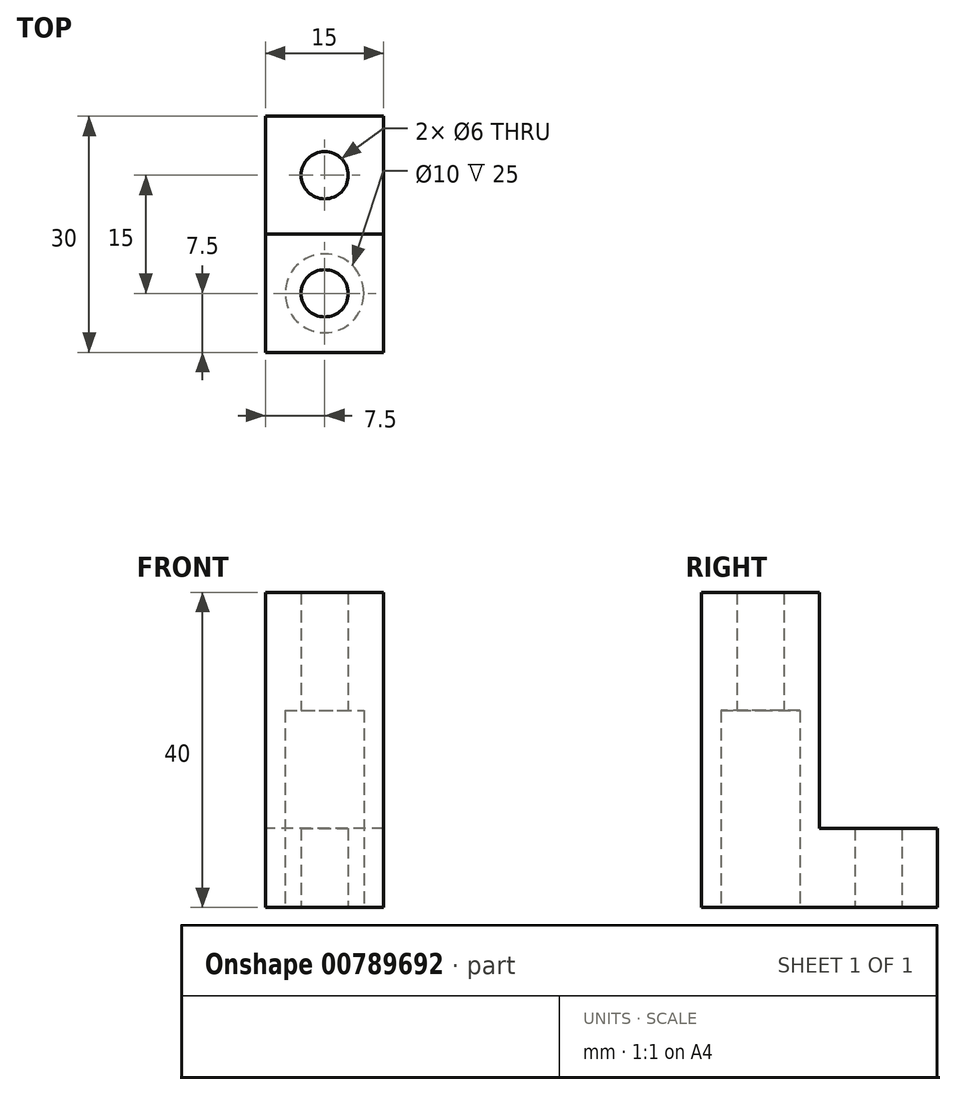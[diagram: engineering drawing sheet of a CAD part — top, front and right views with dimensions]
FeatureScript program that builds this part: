
annotation { "Feature Type Name" : "Feature", "Feature Type Description" : "" }
export const myFeature = defineFeature(function(context is Context, id is Id, definition is map)
    precondition{}
    {
        {
            var Q0;
            Q0=qCreatedBy(makeId("Top.planeOp"),FACE);
            var sketch = newSketch(context, id + "F0", { "sketchPlane" : qUnion([Q0])});
            skLineSegment(sketch, "E0.bottom", {"start": v(7.5, -7.5) * mm, "end": v(-7.5, -7.5) * mm});
            skLineSegment(sketch, "E0.top", {"start": v(7.5, 7.5) * mm, "end": v(-7.5, 7.5) * mm});
            skLineSegment(sketch, "E0.left", {"start": v(7.5, -7.5) * mm, "end": v(7.5, 7.5) * mm});
            skLineSegment(sketch, "E0.right", {"start": v(-7.5, -7.5) * mm, "end": v(-7.5, 7.5) * mm});
            skPoint(sketch, "E0.middle", {"position": v(0, 0) * mm});
            skCircle(sketch, "E1", {"center": v(0, 0) * mm, "radius": 3 * mm});
            skSolve(sketch);
        }
        {
            var Q0;
            Q0 = qSketchRegion(id + "F0", true);
            extrude(context, id + "F1", {"entities" : qUnion([Q0]), "depth" : 40 * mm, "offsetDistance" : 25 * mm});
        }
        {
            var Q0;
            Q0=makeQuery(id+"F1.opExtrude","CAP_FACE",FACE,{"disambiguationData":[OSD([sQuery(id+"F0.wireOp",EDGE,"E0.bottom"),sQuery(id+"F0.wireOp",EDGE,"E0.top"),sQuery(id+"F0.wireOp",EDGE,"E0.left"),sQuery(id+"F0.wireOp",EDGE,"E0.right"),sQuery(id+"F0.wireOp",EDGE,"E1")])],"isStart":true});
            var sketch = newSketch(context, id + "F2", { "sketchPlane" : qUnion([Q0])});
            skLineSegment(sketch, "E2.bottom", {"start": v(7.5, -7.5) * mm, "end": v(-7.5, -7.5) * mm});
            skLineSegment(sketch, "E2.top", {"start": v(7.5, -22.5) * mm, "end": v(-7.5, -22.5) * mm});
            skLineSegment(sketch, "E2.left", {"start": v(7.5, -7.5) * mm, "end": v(7.5, -22.5) * mm});
            skLineSegment(sketch, "E2.right", {"start": v(-7.5, -7.5) * mm, "end": v(-7.5, -22.5) * mm});
            skCircle(sketch, "E3", {"center": v(0, -15) * mm, "radius": 3 * mm});
            skPoint(sketch, "E3.centerSnap0", {"position": v(0, -7.5) * mm});
            skSolve(sketch);
        }
        {
            var Q0;
            Q0 = qSketchRegion(id + "F2", true);
            extrude(context, id + "F3", {"entities" : qUnion([Q0]), "operationType" : NewBodyOperationType.ADD, "oppositeDirection" : true, "depth" : 10 * mm, "offsetDistance" : 25 * mm});
        }
        {
            var Q0;
            Q0=makeQuery(id+"F3.boolean.opBoolean","MERGE",FACE,{"derivedFrom":[makeQuery(id+"F1.opExtrude","CAP_FACE",FACE,{"disambiguationData":[OSD([sQuery(id+"F0.wireOp",EDGE,"E0.bottom"),sQuery(id+"F0.wireOp",EDGE,"E0.top"),sQuery(id+"F0.wireOp",EDGE,"E0.left"),sQuery(id+"F0.wireOp",EDGE,"E0.right"),sQuery(id+"F0.wireOp",EDGE,"E1")])],"isStart":true}),makeQuery(id+"F3.opExtrude","CAP_FACE",FACE,{"disambiguationData":[OSD([sQuery(id+"F2.wireOp",EDGE,"E2.bottom"),sQuery(id+"F2.wireOp",EDGE,"E2.top"),sQuery(id+"F2.wireOp",EDGE,"E2.left"),sQuery(id+"F2.wireOp",EDGE,"E2.right"),sQuery(id+"F2.wireOp",EDGE,"E3")])],"isStart":true})]});
            var sketch = newSketch(context, id + "F4", { "sketchPlane" : qUnion([Q0])});
            skCircle(sketch, "E4", {"center": v(0, 0) * mm, "radius": 5 * mm});
            skSolve(sketch);
        }
        {
            var Q0;
            Q0 = qSketchRegion(id + "F4", true);
            extrude(context, id + "F5", {"entities" : qUnion([Q0]), "operationType" : NewBodyOperationType.REMOVE, "oppositeDirection" : true, "depth" : 25 * mm, "offsetDistance" : 25 * mm});
        }
    });
